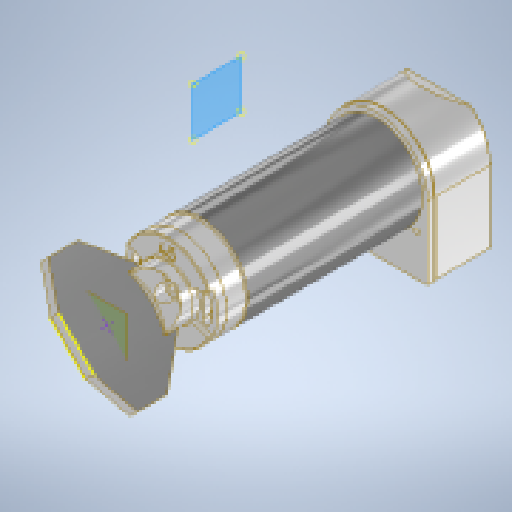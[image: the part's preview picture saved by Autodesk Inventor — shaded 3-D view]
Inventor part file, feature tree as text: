
AUTODESK INVENTOR PART (.ipt)
format: ipt  version: 2024 (Build 280153000, 153)  size: 2,288,128 bytes
history: native  units: mm
features: other x3, sketch x2
ambient origin geometry x8: Origin, YZ Plane, XZ Plane, XY Plane, X Axis, Y Axis, Z Axis, Center Point
bodies: Body1 (feature_tree), Body2 (feature_tree), Body3 (feature_tree), Body4 (feature_tree), Body5 (feature_tree), Body6 (feature_tree), Body7 (feature_tree), Body8 (feature_tree), Body9 (feature_tree), Body10 (feature_tree), Body11 (feature_tree), Body12 (feature_tree), Body13 (feature_tree), Body14 (feature_tree), Body15 (feature_tree), Body16 (feature_tree), Body17 (feature_tree), Body18 (feature_tree), Body19 (feature_tree), Body20 (feature_tree), Body21 (feature_tree), Body22 (feature_tree), Body23 (feature_tree), Body24 (feature_tree), Body25 (feature_tree), Body26 (feature_tree), Body27 (feature_tree), Body28 (feature_tree), Body29 (feature_tree), Body30 (feature_tree), Body31 (feature_tree), Body32 (feature_tree), Body33 (feature_tree), Body34 (feature_tree), Body35 (feature_tree), Body36 (feature_tree), Body37 (feature_tree), Body38 (feature_tree), Body39 (feature_tree), Body40 (feature_tree), Body41 (feature_tree), Body42 (feature_tree), Body43 (feature_tree), Body44 (feature_tree), Body45 (feature_tree)
feature tree (5):
  sketch  "Sketch1"  dims[d0=7.5mm]
  sketch  "Sketch2"  dims[d1=7.5mm]
  other  "ScanningPlane"
  other  "Composite1"
  other  "Srf1"
